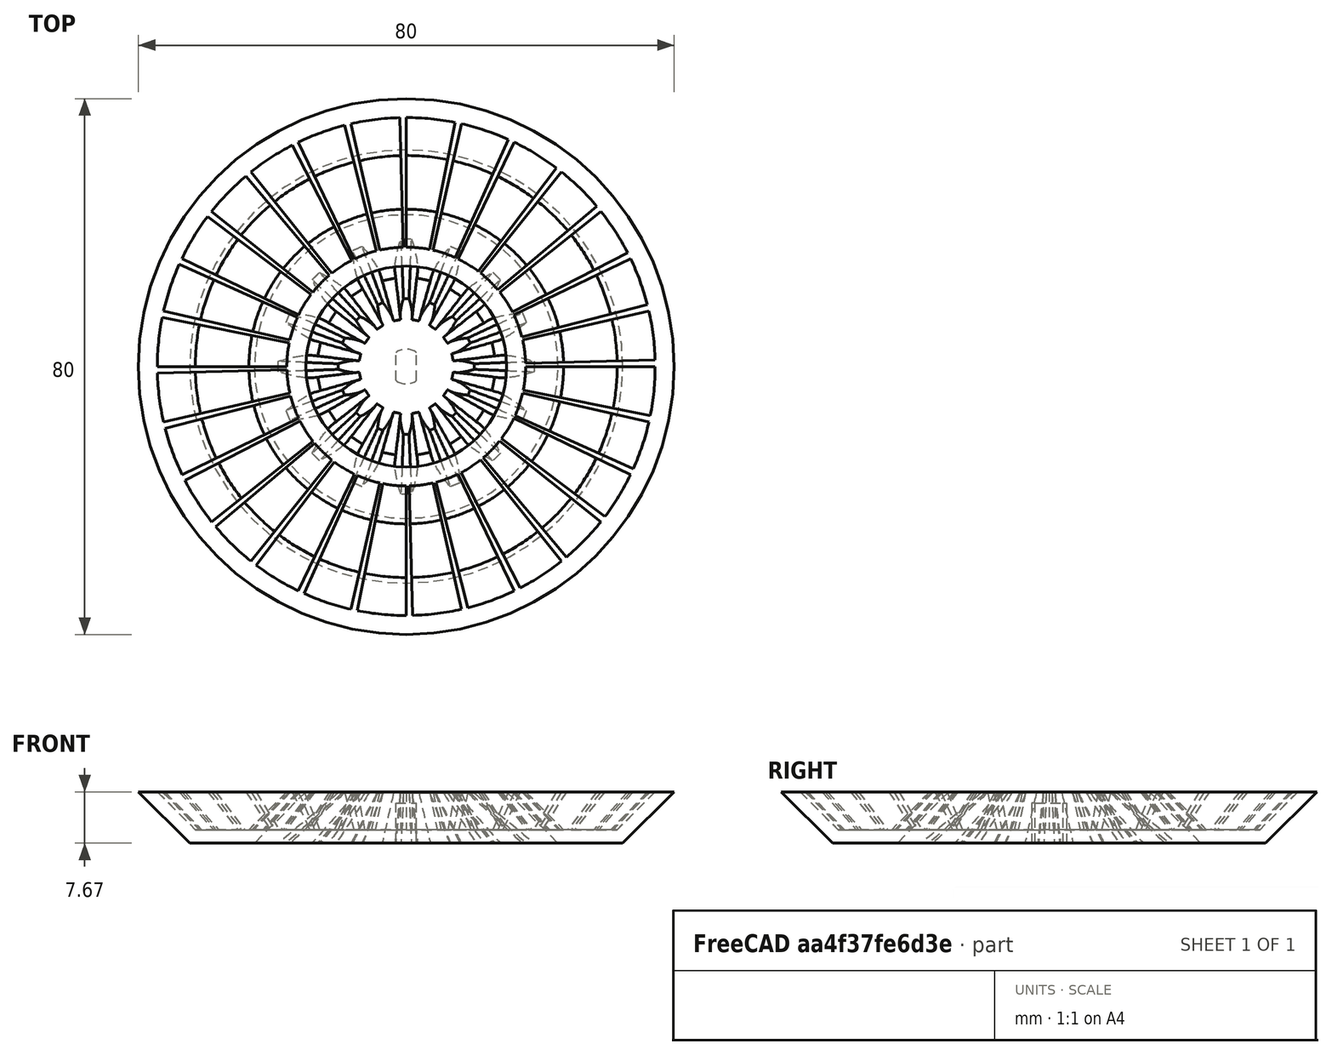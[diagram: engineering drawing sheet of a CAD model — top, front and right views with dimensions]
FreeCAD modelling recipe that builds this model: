
FCSTD DOCUMENT  (FreeCAD 1.1R42925 (Git))
Label: drug_dispenser
License: All rights reserved
LicenseURL: https://en.wikipedia.org/wiki/All_rights_reserved
objects: Sketcher::SketchObject×3, App::Point×2, PartDesign::Body×2, PartDesign::Revolution×2, Part::FeaturePython×1, PartDesign::FeatureBase×1, PartDesign::Pocket×1, Part::DatumPlane×1, PartDesign::PolarPattern×1, Measure::MeasurePython×1, Measure::MeasureArea×1, App::DocumentObjectGroup×1, Mesh::Feature×1, Part::Feature×1
note: 23 computed .brp shape members not serialized (recipe doc carries the construction recipe); baked Part::Feature solids carry a one-line shape summary decoded from their .brp

FEATURE [App::Point] Origin001
  Role = Origin
FEATURE [Sketcher::SketchObject] Sketch001
  ArcFitTolerance = 1e-06
  ExternalTypes = [0]
  FullyConstrained = true
  MakeInternals = false
  MapMode = 5
  Placement = pos=(0,0,0) rot=(1,0,0;3.14159rad)
  expr: Constraints[10] = 3.1
  expr: Constraints[11] = 2.6
  sketch-geometry (4):
    g0: LineSegment StartX=-1.55 StartY=2.08746 StartZ=0 EndX=-1.55 EndY=-2.08746 EndZ=0
    g1: LineSegment StartX=1.55 StartY=2.08746 StartZ=0 EndX=1.55 EndY=-2.08746 EndZ=0
    g2: ArcOfCircle CenterX=0 CenterY=0 CenterZ=0 NormalX=0 NormalY=0 NormalZ=1 AngleXU=0 Radius=2.6 StartAngle=0.932094 EndAngle=2.2095
    g3: ArcOfCircle CenterX=0 CenterY=0 CenterZ=0 NormalX=0 NormalY=0 NormalZ=1 AngleXU=0 Radius=2.6 StartAngle=4.07369 EndAngle=5.35109
  constraints (12):
    c: Vertical(g1)
    c: Coincident(g2,g-1)
    c: Coincident(g2,g0)
    c: Coincident(g2,g1)
    c: Coincident(g3,g2)
    c: Coincident(g3,g0)
    c: Coincident(g3,g1)
    c: Parallel(g1,g0)
    c: Equal(g1,g0)
    c: Equal(g2,g3)
    c: Distance(g0,g1) = 3.1
    c: Radius(g2) = 2.6
FEATURE [Part::FeaturePython] BevelGear  # WARN: FeaturePython — macro-defined, semantics opaque (R4)
  AttacherType = Attacher::AttachEngine3D
  angular_backlash = 0
  backlash = 0
  beta = 0
  clearance = 0.1
  dw = 32
  height = 7.5
  module = 2
  num_teeth = 16
  numpoints = 20
  pitch_angle = 45
  pressure_angle = 20
  reset_origin = true
  version = 1.3.0
  expr: angular_backlash = backlash / dw * 360 ° / pi
  expr: dw = num_teeth * module
  expr: height = 7.5
  expr: module = 2
  expr: num_teeth = 16
FEATURE [PartDesign::FeatureBase] BaseFeature
  BaseFeature = -> BevelGear
  Suppressed = false
FEATURE [PartDesign::Pocket] Pocket
  BaseFeature = -> BaseFeature
  Direction = (0,0,1)
  Length = 6
  Length2 = 5
  Profile = -> Sketch001
  ReferenceAxis = -> Sketch001 [N_Axis]
  Refine = true
  Suppressed = false
  Type = 0
  expr: Length = 6
FEATURE [PartDesign::Body] Body  label="stepper_motor_gear"
  AllowCompound = false
  BaseFeature = -> BevelGear
  Group = -> [BaseFeature,Sketch001,Pocket]
  Origin = -> Origin
  Tip = -> Pocket
FEATURE [App::Point] Origin003
  Role = Origin
FEATURE [Sketcher::SketchObject] Sketch
  ArcFitTolerance = 1e-06
  AttachmentSupport = -> [Origin002]
  ExternalTypes = [0]
  FullyConstrained = true
  MakeInternals = false
  MapMode = 5
  Placement = pos=(0,0,0) rot=(0.57735,0.57735,0.57735;2.0944rad)
  expr: Constraints[17] = 45
  expr: Constraints[18] = 45
  expr: Constraints[19] = 2
  expr: Constraints[20] = 25
  expr: Constraints[21] = 2
  expr: Constraints[23] = 15
  sketch-geometry (8):
    g0: LineSegment StartX=15 StartY=7.66548 StartZ=0 EndX=22.6655 EndY=0 EndZ=0
    g1: LineSegment StartX=22.6655 StartY=0 StartZ=0 EndX=32.3345 EndY=0 EndZ=0
    g2: LineSegment StartX=32.3345 StartY=0 StartZ=0 EndX=40 EndY=7.66548 EndZ=0
    g3: LineSegment StartX=40 StartY=7.66548 StartZ=0 EndX=37.1716 EndY=7.66548 EndZ=0
    g4: LineSegment StartX=37.1716 StartY=7.66548 StartZ=0 EndX=31.5061 EndY=2 EndZ=0
    g5: LineSegment StartX=31.5061 StartY=2 StartZ=0 EndX=23.4939 EndY=2 EndZ=0
    g6: LineSegment StartX=17.8284 StartY=7.66548 StartZ=0 EndX=23.4939 EndY=2 EndZ=0
    g7: LineSegment StartX=17.8284 StartY=7.66548 StartZ=0 EndX=15 EndY=7.66548 EndZ=0
  constraints (24):
    c: PointOnObject(g0,g-1)
    c: Coincident(g1,g0)
    c: PointOnObject(g1,g-1)
    c: Coincident(g2,g1)
    c: Coincident(g3,g2)
    c: Horizontal(g3)
    c: Coincident(g4,g3)
    c: Coincident(g5,g4)
    c: Horizontal(g5)
    c: Coincident(g6,g5)
    c: Coincident(g7,g6)
    c: Coincident(g7,g0)
    c: Parallel(g7,g3)
    c: PointOnObject(g6,g3)
    c: Parallel(g4,g2)
    c: Parallel(g6,g0)
    c: Equal(g3,g7)
    c: Angle(g-1,g2) = 0.785398
    c: Angle(g0,g-1) = 0.785398
    c: Distance(g2,g4) = 2
    c: DistanceX(g0,g2) = 25
    c: Distance(g1,g5) = 2
    c: Equal(g5,g4)
    c: DistanceX(g-1,g0) = 15
FEATURE [PartDesign::Revolution] Revolution
  Angle = 360
  Angle2 = 60
  Axis = (0,0,1)
  Base = (0,0,0)
  Profile = -> Sketch
  ReferenceAxis = -> Sketch [V_Axis]
  Refine = true
  Reversed = true
  Suppressed = false
  Type = 0
FEATURE [Part::DatumPlane] DatumPlane
  AttachmentSupport = -> [Revolution]
  MapMode = 7
  Placement = pos=(0,37.1716,7.66548) rot=(0.57735,-0.57735,-0.57735;2.0944rad)
FEATURE [Sketcher::SketchObject] Sketch002
  ArcFitTolerance = 1e-06
  AttachmentSupport = -> [DatumPlane]
  ExternalGeometry = -> [Revolution]
  ExternalTypes = [0,0,0,0]
  FullyConstrained = true
  MakeInternals = false
  MapMode = 5
  Placement = pos=(0,37.1716,7.66548) rot=(0.57735,-0.57735,-0.57735;2.0944rad)
  sketch-geometry (2):
    g0: LineSegment StartX=5.66548 StartY=-5.66548 StartZ=0 EndX=13.6777 EndY=-5.66548 EndZ=0
    g1: LineSegment StartX=0 StartY=0 StartZ=0 EndX=19.3431 EndY=0 EndZ=0
  constraints (4):
    c: Coincident(g0,g-5)
    c: Coincident(g0,g-4)
    c: Coincident(g1,g-5)
    c: Coincident(g1,g-4)
FEATURE [PartDesign::Revolution] Revolution001
  Angle = 1.5
  Angle2 = 60
  Axis = (1e-16,1e-16,1)
  Base = (0,0,0)
  BaseFeature = -> Revolution
  Profile = -> Sketch002
  ReferenceAxis = -> Z_Axis001
  Refine = true
  Suppressed = false
  Type = 0
  expr: Angle = 1.5
FEATURE [PartDesign::PolarPattern] PolarPattern
  Angle = 360
  Axis = -> Z_Axis001
  BaseFeature = -> Revolution001
  Mode = 0
  Occurrences = 28
  Offset = 120
  Originals = -> [Revolution001]
  Refine = true
  Suppressed = false
  TransformMode = 0
  expr: Occurrences = 28
FEATURE [PartDesign::Body] Body001  label="Body"
  AllowCompound = false
  Group = -> [Sketch,Revolution,DatumPlane,Sketch002,Revolution001,PolarPattern]
  Origin = -> Origin002
  Tip = -> PolarPattern
FEATURE [Measure::MeasurePython] Center_of_mass  label="Center_of_mass: COM
X: -0.00 mm
Y: 0.00 mm
Z: 3.52 mm"  # WARN: FeaturePython — macro-defined, semantics opaque (R4)
  Element = -> Body001 [PolarPattern.]
  Placement = pos=(-6e-15,3.9e-15,3.51995) rot=(0,0,1;0rad)
  Result = (-6e-15,3.9e-15,3.51995)
FEATURE [Measure::MeasureArea] Area  label="Area: 24.63 cm^2"
  Area = 2463.48
  Elements = -> [Body001]
FEATURE [App::DocumentObjectGroup] Measurements
  Group = -> [Center_of_mass,Area]
FEATURE [Mesh::Feature] Round_Display_shell_3D_Model  label="Round-Display-shell-3D-Model"
FEATURE [Part::Feature] Round_Display_shell_3D_Model001
  shape: large baked B-rep (97 MB .brp); summary skipped
